MODEL slx_88a6a4993d81
CONFIG AbsTol = auto
CONFIG EnableMultiTasking = off
CONFIG FixedStep = auto
CONFIG MaxStep = auto
CONFIG MinStep = auto
CONFIG RelTol = 1e-3
CONFIG SampleTimeConstraint = Unconstrained
CONFIG Solver = VariableStepAuto
CONFIG SolverName = VariableStepAuto
CONFIG StartTime = 0.0
CONFIG StopTime = 10.0
BLOCK [Display] Display
  Decimation = 1
  Ports = [1]
BLOCK [Display] Display1
  Decimation = 1
  Ports = [1]
BLOCK [Display] Display2
  Decimation = 1
  Ports = [1]
BLOCK [SubSystem] Subsystem
  Ports = [3, 3]
  RequestExecContextInheritance = off
BLOCK [Sin] Subsystem/CoSine Wave Function2
  Phase = 1.57079
  Ports = [1, 1]
  SampleTime = 0
  TimeSource = Use external signal
BLOCK [Sin] Subsystem/CoSine Wave Function3
  Phase = 1.57079
  Ports = [1, 1]
  SampleTime = 0
  TimeSource = Use external signal
BLOCK [Sin] Subsystem/CoSine Wave Function4
  Phase = 1.57079
  Ports = [1, 1]
  SampleTime = 0
  TimeSource = Use external signal
BLOCK [Constant] Subsystem/Constant
BLOCK [Constant] Subsystem/Constant1
BLOCK [Constant] Subsystem/Constant2
BLOCK [Constant] Subsystem/Constant3
  Value = 90
BLOCK [From] Subsystem/From
  GotoTag = p2
  TagVisibility = global
BLOCK [From] Subsystem/From1
  GotoTag = p3
  TagVisibility = global
BLOCK [From] Subsystem/From2
  GotoTag = p3
  TagVisibility = global
BLOCK [From] Subsystem/From3
  GotoTag = p1
  TagVisibility = global
BLOCK [From] Subsystem/From4
  GotoTag = p2
  TagVisibility = global
BLOCK [Gain] Subsystem/Gain
  Gain = -1
  OutDataTypeStr = Inherit: Inherit via internal rule
  ParamDataTypeStr = Inherit: Inherit via internal rule
  SaturateOnIntegerOverflow = off
BLOCK [Goto] Subsystem/Goto
  GotoTag = p1
  TagVisibility = global
BLOCK [Goto] Subsystem/Goto1
  GotoTag = p2
  TagVisibility = global
BLOCK [Goto] Subsystem/Goto2
  GotoTag = p3
  TagVisibility = global
BLOCK [Product] Subsystem/Product
  InputSameDT = off
  OutDataTypeStr = Inherit: Inherit via internal rule
  Ports = [2, 1]
  RndMeth = Floor
  SaturateOnIntegerOverflow = off
BLOCK [Product] Subsystem/Product1
  InputSameDT = off
  OutDataTypeStr = Inherit: Inherit via internal rule
  Ports = [2, 1]
  RndMeth = Floor
  SaturateOnIntegerOverflow = off
BLOCK [Product] Subsystem/Product2
  InputSameDT = off
  OutDataTypeStr = Inherit: Inherit via internal rule
  Ports = [2, 1]
  RndMeth = Floor
  SaturateOnIntegerOverflow = off
BLOCK [Product] Subsystem/Product3
  InputSameDT = off
  OutDataTypeStr = Inherit: Inherit via internal rule
  Ports = [2, 1]
  RndMeth = Floor
  SaturateOnIntegerOverflow = off
BLOCK [Product] Subsystem/Product4
  InputSameDT = off
  OutDataTypeStr = Inherit: Inherit via internal rule
  Ports = [2, 1]
  RndMeth = Floor
  SaturateOnIntegerOverflow = off
BLOCK [Product] Subsystem/Product5
  InputSameDT = off
  OutDataTypeStr = Inherit: Inherit via internal rule
  Ports = [2, 1]
  RndMeth = Floor
  SaturateOnIntegerOverflow = off
BLOCK [Sin] Subsystem/Sine Wave Function
  Ports = [1, 1]
  SampleTime = 0
  TimeSource = Use external signal
BLOCK [Sin] Subsystem/Sine Wave Function1
  Ports = [1, 1]
  SampleTime = 0
  TimeSource = Use external signal
BLOCK [Sin] Subsystem/Sine Wave Function2
  Ports = [1, 1]
  SampleTime = 0
  TimeSource = Use external signal
BLOCK [Sum] Subsystem/Sum
  IconShape = round
  InputSameDT = off
  Inputs = |++
  OutDataTypeStr = Inherit: Inherit via internal rule
  Ports = [2, 1]
  SaturateOnIntegerOverflow = off
BLOCK [Sum] Subsystem/Sum1
  IconShape = round
  InputSameDT = off
  Inputs = |+-
  OutDataTypeStr = Inherit: Inherit via internal rule
  Ports = [2, 1]
  SaturateOnIntegerOverflow = off
BLOCK [Sum] Subsystem/Sum2
  InputSameDT = off
  Inputs = |+++
  OutDataTypeStr = Inherit: Inherit via internal rule
  Ports = [3, 1]
  SaturateOnIntegerOverflow = off
BLOCK [Inport] Subsystem/fi1
  IconDisplay = Port number
BLOCK [Inport] Subsystem/fi2
  IconDisplay = Port number
  Port = 2
BLOCK [Inport] Subsystem/fi3
  IconDisplay = Port number
  Port = 3
BLOCK [Outport] Subsystem/x
  IconDisplay = Port number
BLOCK [Outport] Subsystem/y
  IconDisplay = Port number
  Port = 2
BLOCK [Outport] Subsystem/z
  IconDisplay = Port number
  Port = 3
LINE Subsystem/CoSine Wave Function2:1 -> Subsystem/Product1:1
LINE Subsystem/CoSine Wave Function3:1 -> Subsystem/Product:2
LINE Subsystem/CoSine Wave Function4:1 -> Subsystem/Product2:1
LINE Subsystem/Constant1:1 -> Subsystem/Goto2:1
LINE Subsystem/Constant2:1 -> Subsystem/Goto:1
LINE Subsystem/Constant3:1 -> Subsystem/Sum1:1
LINE Subsystem/Constant:1 -> Subsystem/Goto1:1
LINE Subsystem/From1:1 -> Subsystem/Product1:2
LINE Subsystem/From2:1 -> Subsystem/Product4:1
LINE Subsystem/From3:1 -> Subsystem/Sum2:1
LINE Subsystem/From4:1 -> Subsystem/Product5:1
LINE Subsystem/From:1 -> Subsystem/Product:1
LINE Subsystem/Gain:1 -> Subsystem/CoSine Wave Function2:1
LINE Subsystem/Gain:1 -> Subsystem/Sine Wave Function1:1
LINE Subsystem/Product1:1 -> Subsystem/Sum:2
LINE Subsystem/Product2:1 -> Subsystem/x:1
LINE Subsystem/Product3:1 -> Subsystem/y:1
LINE Subsystem/Product4:1 -> Subsystem/Sum2:2
LINE Subsystem/Product5:1 -> Subsystem/Sum2:3
LINE Subsystem/Product:1 -> Subsystem/Sum:1
LINE Subsystem/Sine Wave Function1:1 -> Subsystem/Product4:2
LINE Subsystem/Sine Wave Function2:1 -> Subsystem/Product5:2
LINE Subsystem/Sine Wave Function:1 -> Subsystem/Product3:1
LINE Subsystem/Sum1:1 -> Subsystem/CoSine Wave Function3:1
LINE Subsystem/Sum1:1 -> Subsystem/Sine Wave Function2:1
LINE Subsystem/Sum2:1 -> Subsystem/z:1
LINE Subsystem/Sum:1 -> Subsystem/Product2:2
LINE Subsystem/Sum:1 -> Subsystem/Product3:2
LINE Subsystem/fi1:1 -> Subsystem/CoSine Wave Function4:1
LINE Subsystem/fi1:1 -> Subsystem/Sine Wave Function:1
LINE Subsystem/fi2:1 -> Subsystem/Sum1:2
LINE Subsystem/fi3:1 -> Subsystem/Gain:1
LINE Subsystem:1 -> Display:1
LINE Subsystem:2 -> Display1:1
LINE Subsystem:3 -> Display2:1
